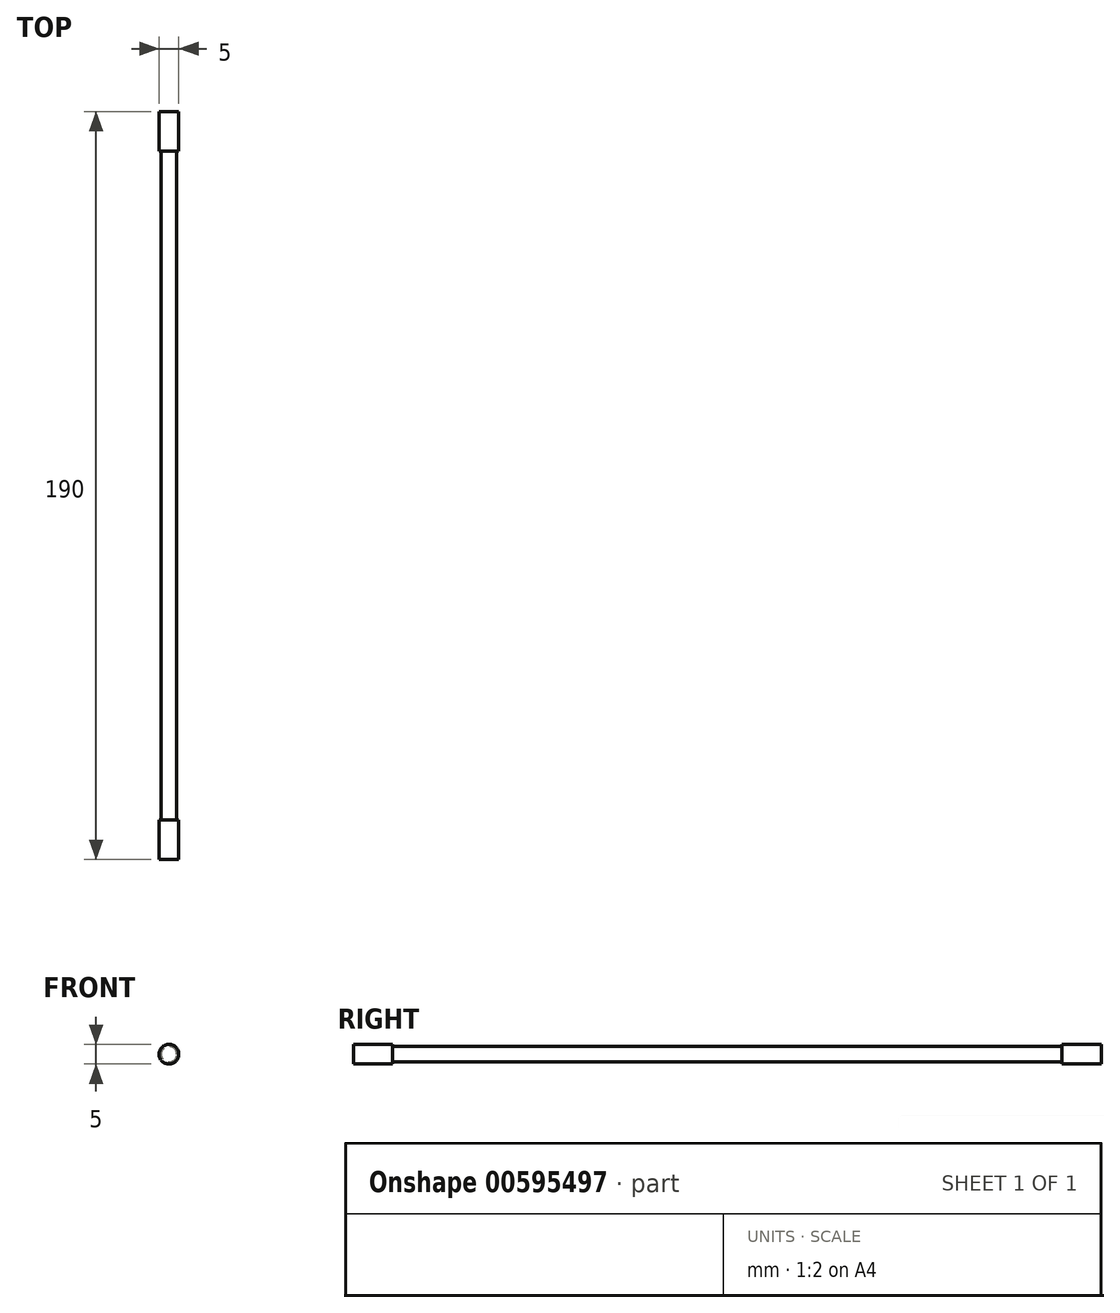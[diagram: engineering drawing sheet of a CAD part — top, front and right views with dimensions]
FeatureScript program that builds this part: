
annotation { "Feature Type Name" : "Feature", "Feature Type Description" : "" }
export const myFeature = defineFeature(function(context is Context, id is Id, definition is map)
    precondition{}
    {
        {
            var Q0;
            Q0=qCreatedBy(makeId("Front.planeOp"),FACE);
            var sketch = newSketch(context, id + "F0", { "sketchPlane" : qUnion([Q0])});
            skCircle(sketch, "E0", {"center": v(0, 0) * mm, "radius": 2.5 * mm});
            skSolve(sketch);
        }
        {
            var Q0;
            Q0=makeQuery(id+"F0.imprint","IMPRINT",FACE,{"disambiguationData":[TD([[makeQuery(id+"F0.imprint","IMPRINT",EDGE,{"derivedFrom":sQuery(id+"F0.wireOp",EDGE,"E0")}),1.0]])]});
            extrude(context, id + "F1", {"entities" : qUnion([Q0]), "oppositeDirection" : true, "depth" : 10 * mm, "offsetDistance" : 25 * mm});
        }
        {
            var Q0;
            Q0=makeQuery(id+"F1.opExtrude","CAP_FACE",FACE,{"disambiguationData":[OSD([sQuery(id+"F0.wireOp",EDGE,"E0")])],"isStart":false});
            var sketch = newSketch(context, id + "F2", { "sketchPlane" : qUnion([Q0])});
            skCircle(sketch, "E1", {"center": v(0, 0) * mm, "radius": 2 * mm});
            skSolve(sketch);
        }
        {
            var Q0;
            Q0=makeQuery(id+"F2.imprint","IMPRINT",FACE,{"disambiguationData":[TD([[makeQuery(id+"F2.imprint","IMPRINT",EDGE,{"derivedFrom":sQuery(id+"F2.wireOp",EDGE,"E1")}),1.0]])]});
            extrude(context, id + "F3", {"entities" : qUnion([Q0]), "operationType" : NewBodyOperationType.ADD, "depth" : 170 * mm, "offsetDistance" : 25 * mm});
        }
        {
            var Q0;
            Q0=makeQuery(id+"F3.opExtrude","CAP_FACE",FACE,{"disambiguationData":[OSD([sQuery(id+"F2.wireOp",EDGE,"E1")])],"isStart":false});
            var sketch = newSketch(context, id + "F4", { "sketchPlane" : qUnion([Q0])});
            skCircle(sketch, "E2", {"center": v(0, 0) * mm, "radius": 2.5 * mm});
            skSolve(sketch);
        }
        {
            var Q0;
            Q0=makeQuery(id+"F4.imprint","IMPRINT",FACE,{"disambiguationData":[TD([[makeQuery(id+"F4.imprint","IMPRINT",EDGE,{"derivedFrom":makeQuery(id+"F3.opExtrude","CAP_EDGE",EDGE,{"disambiguationData":[OSD([sQuery(id+"F2.wireOp",EDGE,"E1")])],"isStart":false})}),1.0]])]});
            var Q1;
            Q1=makeQuery(id+"F4.imprint","IMPRINT",FACE,{"disambiguationData":[TD([[makeQuery(id+"F4.imprint","IMPRINT",EDGE,{"derivedFrom":sQuery(id+"F4.wireOp",EDGE,"E2")}),1.0]])]});
            extrude(context, id + "F5", {"entities" : qUnion([Q0, Q1]), "operationType" : NewBodyOperationType.ADD, "depth" : 10 * mm, "offsetDistance" : 25 * mm});
        }
    });
